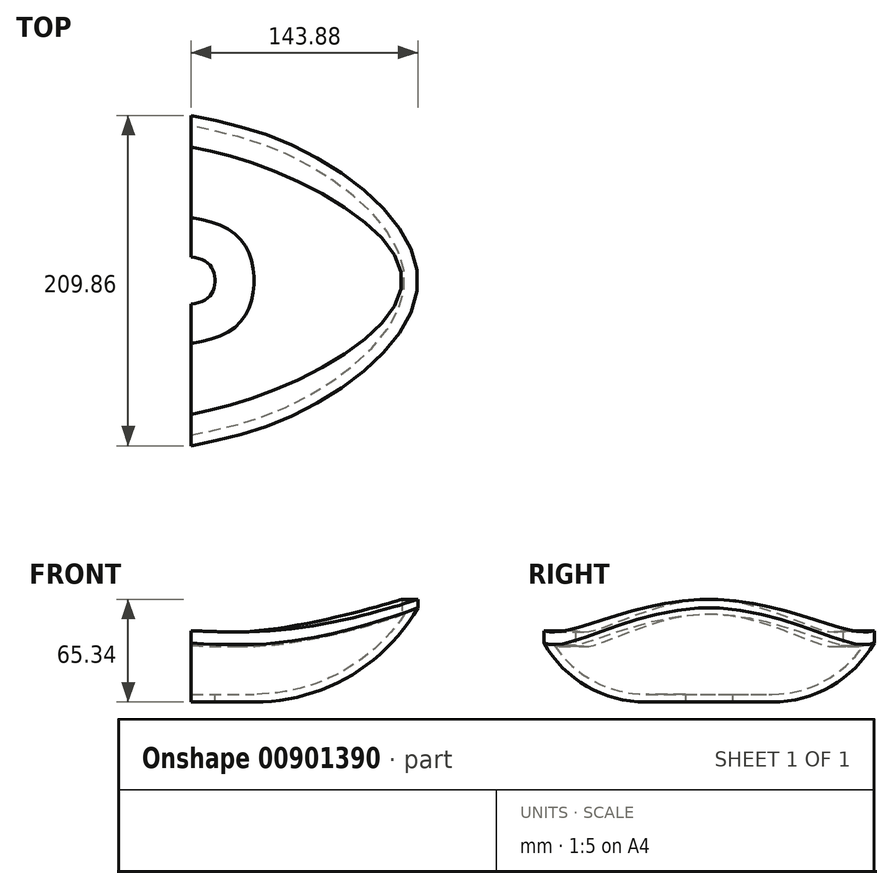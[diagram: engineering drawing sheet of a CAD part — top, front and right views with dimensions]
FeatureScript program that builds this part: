
annotation { "Feature Type Name" : "Feature", "Feature Type Description" : "" }
export const myFeature = defineFeature(function(context is Context, id is Id, definition is map)
    precondition{}
    {
        {
            var Q0;
            Q0=qCreatedBy(makeId("Front.planeOp"),FACE);
            var sketch = newSketch(context, id + "F0", { "sketchPlane" : qUnion([Q0])});
            skLineSegment(sketch, "E0.bottom", {"start": v(15, 5) * mm, "end": v(40, 5) * mm});
            skLineSegment(sketch, "E0.top", {"start": v(15, 0) * mm, "end": v(40, 0) * mm});
            skLineSegment(sketch, "E0.left", {"start": v(15, 5) * mm, "end": v(15, 0) * mm});
            skLineSegment(sketch, "E0.right", {"start": v(40, 5) * mm, "end": v(40, 0) * mm, "construction": true});
            skLineSegment(sketch, "E1.bottom", {"start": v(133.88, 65.34) * mm, "end": v(143.88, 65.34) * mm});
            skLineSegment(sketch, "E1.top", {"start": v(133.88, 56.06) * mm, "end": v(135.58, 56.06) * mm});
            skLineSegment(sketch, "E1.left", {"start": v(133.88, 65.34) * mm, "end": v(133.88, 56.06) * mm});
            skLineSegment(sketch, "E1.right", {"start": v(143.88, 65.34) * mm, "end": v(143.88, 56.06) * mm});
            skArc(sketch, "E2", {"start": v(40, 0) * mm, "mid": v(99.97, 16.06) * mm, "end": v(143.88, 59.93) * mm});
            skArc(sketch, "E3", {"start": v(40, 5) * mm, "mid": v(94.18, 18.56) * mm, "end": v(135.58, 56.06) * mm});
            skLineSegment(sketch, "E4.trimOffspring", {"start": v(141.54, 56.06) * mm, "end": v(143.88, 56.06) * mm});
            skLineSegment(sketch, "E5", {"start": v(0, 0) * mm, "end": v(0, 50) * mm, "construction": true});
            skSolve(sketch);
        }
        {
            var Q0;
            Q0=sQuery(id+"F0.wireOp",EDGE,"E5");
            var Q1;
            Q1 = qBodyType(qCreatedBy(id + "F2" ,EDGE), BodyType.WIRE);
            cPlane(context, id + "F1", {"entities" : qUnion([Q0, Q1]), "cplaneType" : CPlaneType.LINE_ANGLE, "offset" : 25 * mm, "angle" : 30 * degree, "oppositeDirection" : true, "width" : 150 * mm, "height" : 150 * mm});
        }
        {
            var Q0;
            Q0=qCreatedBy(id+"F1.planeOp",FACE);
            var sketch = newSketch(context, id + "F2", { "sketchPlane" : qUnion([Q0])});
            skLineSegment(sketch, "E6.bottom", {"start": v(15, 5) * mm, "end": v(40, 5) * mm});
            skLineSegment(sketch, "E6.top", {"start": v(15, 0) * mm, "end": v(40, 0) * mm});
            skLineSegment(sketch, "E6.left", {"start": v(15, 5) * mm, "end": v(15, 0) * mm});
            skLineSegment(sketch, "E6.right", {"start": v(40, 5) * mm, "end": v(40, 0) * mm, "construction": true});
            skLineSegment(sketch, "E7.bottom", {"start": v(84.93, 45.36) * mm, "end": v(104.93, 45.36) * mm});
            skLineSegment(sketch, "E7.top", {"start": v(84.93, 36.08) * mm, "end": v(98.18, 36.08) * mm});
            skLineSegment(sketch, "E7.left", {"start": v(84.93, 45.36) * mm, "end": v(84.93, 36.08) * mm});
            skLineSegment(sketch, "E7.right", {"start": v(104.93, 45.36) * mm, "end": v(104.93, 36.08) * mm});
            skArc(sketch, "E8", {"start": v(40, 0) * mm, "mid": v(77.48, 10.04) * mm, "end": v(104.93, 37.46) * mm});
            skArc(sketch, "E9", {"start": v(40, 5) * mm, "mid": v(72.98, 13.26) * mm, "end": v(98.18, 36.08) * mm});
            skLineSegment(sketch, "E10.trimOffspring", {"start": v(104.1, 36.08) * mm, "end": v(104.93, 36.08) * mm});
            skLineSegment(sketch, "E11", {"start": v(0, 0) * mm, "end": v(0, 50) * mm, "construction": true});
            skSolve(sketch);
        }
        {
            var Q0;
            Q0=sQuery(id+"F2.wireOp",EDGE,"E11");
            cPlane(context, id + "F3", {"entities" : qUnion([Q0]), "cplaneType" : CPlaneType.LINE_ANGLE, "offset" : 25 * mm, "angle" : 150 * degree, "oppositeDirection" : true, "width" : 150 * mm, "height" : 150 * mm});
        }
        {
            var Q0;
            Q0=qCreatedBy(id+"F3.planeOp",FACE);
            var sketch = newSketch(context, id + "F4", { "sketchPlane" : qUnion([Q0])});
            skLineSegment(sketch, "E12.bottom", {"start": v(15, 5) * mm, "end": v(40, 5) * mm});
            skLineSegment(sketch, "E12.top", {"start": v(15, 0) * mm, "end": v(40, 0) * mm});
            skLineSegment(sketch, "E12.left", {"start": v(15, 5) * mm, "end": v(15, 0) * mm});
            skLineSegment(sketch, "E12.right", {"start": v(40, 5) * mm, "end": v(40, 0) * mm, "construction": true});
            skLineSegment(sketch, "E13.bottom", {"start": v(84.93, 45.36) * mm, "end": v(104.93, 45.36) * mm});
            skLineSegment(sketch, "E13.top", {"start": v(84.93, 36.08) * mm, "end": v(98.18, 36.08) * mm});
            skLineSegment(sketch, "E13.left", {"start": v(84.93, 45.36) * mm, "end": v(84.93, 36.08) * mm});
            skLineSegment(sketch, "E13.right", {"start": v(104.93, 45.36) * mm, "end": v(104.93, 36.08) * mm});
            skArc(sketch, "E14", {"start": v(40, 0) * mm, "mid": v(77.48, 10.04) * mm, "end": v(104.93, 37.46) * mm});
            skArc(sketch, "E15", {"start": v(40, 5) * mm, "mid": v(72.98, 13.26) * mm, "end": v(98.18, 36.08) * mm});
            skLineSegment(sketch, "E16.trimOffspring", {"start": v(104.1, 36.08) * mm, "end": v(104.93, 36.08) * mm});
            skLineSegment(sketch, "E17", {"start": v(0, 0) * mm, "end": v(0, 50) * mm, "construction": true});
            skSolve(sketch);
        }
        {
            var Q0;
            Q0=qCreatedBy(makeId("Right.planeOp"),FACE);
            var sketch = newSketch(context, id + "F5", { "sketchPlane" : qUnion([Q0])});
            skLineSegment(sketch, "E18.bottom", {"start": v(15, 5) * mm, "end": v(40, 5) * mm});
            skLineSegment(sketch, "E18.top", {"start": v(15, 0) * mm, "end": v(40, 0) * mm});
            skLineSegment(sketch, "E18.left", {"start": v(15, 5) * mm, "end": v(15, 0) * mm});
            skLineSegment(sketch, "E18.right", {"start": v(40, 5) * mm, "end": v(40, 0) * mm, "construction": true});
            skLineSegment(sketch, "E19.bottom", {"start": v(84.93, 45.36) * mm, "end": v(104.93, 45.36) * mm});
            skLineSegment(sketch, "E19.top", {"start": v(84.93, 36.08) * mm, "end": v(98.18, 36.08) * mm});
            skLineSegment(sketch, "E19.left", {"start": v(84.93, 45.36) * mm, "end": v(84.93, 36.08) * mm});
            skLineSegment(sketch, "E19.right", {"start": v(104.93, 45.36) * mm, "end": v(104.93, 36.08) * mm});
            skArc(sketch, "E20", {"start": v(40, 0) * mm, "mid": v(77.48, 10.04) * mm, "end": v(104.93, 37.46) * mm});
            skArc(sketch, "E21", {"start": v(40, 5) * mm, "mid": v(72.98, 13.26) * mm, "end": v(98.18, 36.08) * mm});
            skLineSegment(sketch, "E22.trimOffspring", {"start": v(104.1, 36.08) * mm, "end": v(104.93, 36.08) * mm});
            skLineSegment(sketch, "E23", {"start": v(0, 0) * mm, "end": v(0, 50) * mm, "construction": true});
            skSolve(sketch);
        }
        {
            var Q0;
            Q0=sQuery(id+"F5.wireOp",EDGE,"E23");
            cPlane(context, id + "F6", {"entities" : qUnion([Q0]), "cplaneType" : CPlaneType.LINE_ANGLE, "offset" : 25 * mm, "angle" : 180 * degree, "width" : 150 * mm, "height" : 150 * mm});
        }
        {
            var Q0;
            Q0=qCreatedBy(id+"F6.planeOp",FACE);
            var sketch = newSketch(context, id + "F7", { "sketchPlane" : qUnion([Q0])});
            skLineSegment(sketch, "E24.bottom", {"start": v(15, 5) * mm, "end": v(40, 5) * mm});
            skLineSegment(sketch, "E24.top", {"start": v(15, 0) * mm, "end": v(40, 0) * mm});
            skLineSegment(sketch, "E24.left", {"start": v(15, 5) * mm, "end": v(15, 0) * mm});
            skLineSegment(sketch, "E24.right", {"start": v(40, 5) * mm, "end": v(40, 0) * mm, "construction": true});
            skLineSegment(sketch, "E25.bottom", {"start": v(84.93, 45.36) * mm, "end": v(104.93, 45.36) * mm});
            skLineSegment(sketch, "E25.top", {"start": v(84.93, 36.08) * mm, "end": v(98.18, 36.08) * mm});
            skLineSegment(sketch, "E25.left", {"start": v(84.93, 45.36) * mm, "end": v(84.93, 36.08) * mm});
            skLineSegment(sketch, "E25.right", {"start": v(104.93, 45.36) * mm, "end": v(104.93, 36.08) * mm});
            skArc(sketch, "E26", {"start": v(40, 0) * mm, "mid": v(77.48, 10.04) * mm, "end": v(104.93, 37.46) * mm});
            skArc(sketch, "E27", {"start": v(40, 5) * mm, "mid": v(72.98, 13.26) * mm, "end": v(98.18, 36.08) * mm});
            skLineSegment(sketch, "E28.trimOffspring", {"start": v(104.1, 36.08) * mm, "end": v(104.93, 36.08) * mm});
            skLineSegment(sketch, "E29", {"start": v(0, 0) * mm, "end": v(0, 50) * mm, "construction": true});
            skSolve(sketch);
        }
        {
            var Q0;
            Q0=makeQuery(id+"F7.imprint","IMPRINT",FACE,{"disambiguationData":[TD([[makeQuery(id+"F7.imprint","IMPRINT",EDGE,{"derivedFrom":sQuery(id+"F7.wireOp",EDGE,"E24.bottom")}),-1.0]])]});
            var Q1;
            Q1=makeQuery(id+"F4.imprint","IMPRINT",FACE,{"disambiguationData":[TD([[makeQuery(id+"F4.imprint","IMPRINT",EDGE,{"derivedFrom":sQuery(id+"F4.wireOp",EDGE,"E12.bottom")}),-1.0]])]});
            var Q2;
            Q2=makeQuery(id+"F0.imprint","IMPRINT",FACE,{"disambiguationData":[TD([[makeQuery(id+"F0.imprint","IMPRINT",EDGE,{"derivedFrom":sQuery(id+"F0.wireOp",EDGE,"E0.bottom")}),-1.0]])]});
            var Q3;
            Q3=makeQuery(id+"F2.imprint","IMPRINT",FACE,{"disambiguationData":[TD([[makeQuery(id+"F2.imprint","IMPRINT",EDGE,{"derivedFrom":sQuery(id+"F2.wireOp",EDGE,"E6.bottom")}),-1.0]])]});
            var Q4;
            Q4=makeQuery(id+"F5.imprint","IMPRINT",FACE,{"disambiguationData":[TD([[makeQuery(id+"F5.imprint","IMPRINT",EDGE,{"derivedFrom":sQuery(id+"F5.wireOp",EDGE,"E18.bottom")}),-1.0]])]});
            loft(context, id + "F8", {"sheetProfilesArray" : [{ "sheetProfileEntities" : qUnion([Q0]) }, { "sheetProfileEntities" : qUnion([Q1]) }, { "sheetProfileEntities" : qUnion([Q2]) }, { "sheetProfileEntities" : qUnion([Q3]) }, { "sheetProfileEntities" : qUnion([Q4]) }]});
        }
    });
